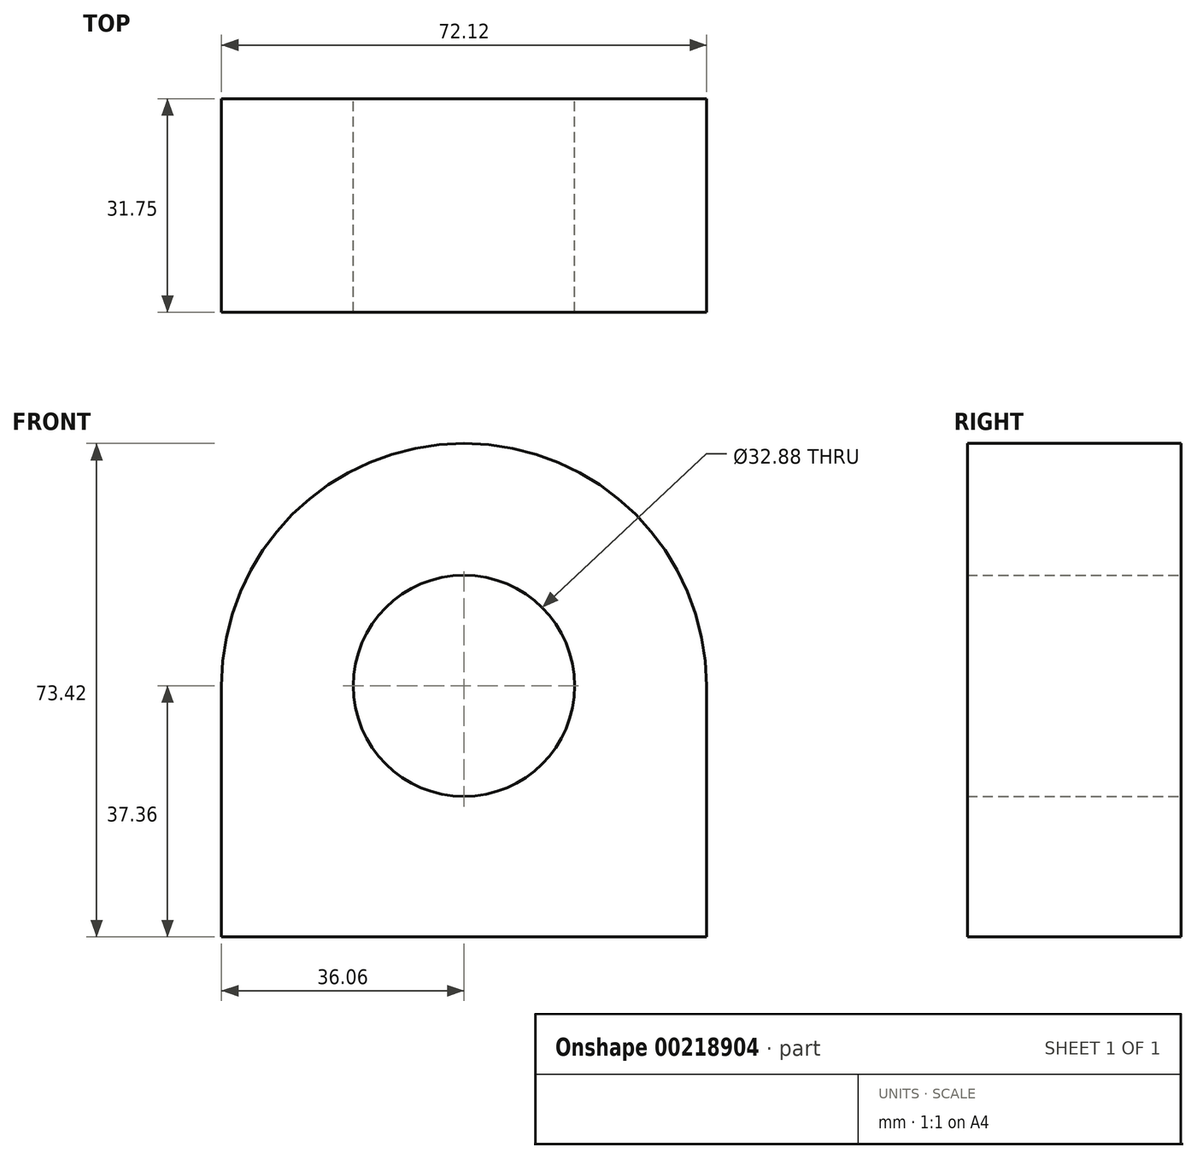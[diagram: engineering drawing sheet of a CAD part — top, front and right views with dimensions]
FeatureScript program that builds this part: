
annotation { "Feature Type Name" : "Feature", "Feature Type Description" : "" }
export const myFeature = defineFeature(function(context is Context, id is Id, definition is map)
    precondition{}
    {
        {
            var Q0;
            Q0=qCreatedBy(makeId("Front.planeOp"),FACE);
            var sketch = newSketch(context, id + "F0", { "sketchPlane" : qUnion([Q0])});
            skLineSegment(sketch, "E0.top", {"start": v(36.06, -18.68) * mm, "end": v(-36.06, -18.68) * mm});
            skLineSegment(sketch, "E0.left", {"start": v(36.06, 18.68) * mm, "end": v(36.06, -18.68) * mm});
            skLineSegment(sketch, "E0.right", {"start": v(-36.06, 18.68) * mm, "end": v(-36.06, -18.68) * mm});
            skPoint(sketch, "E0.middle", {"position": v(0, 0) * mm});
            skArc(sketch, "E1", {"start": v(-36.06, 18.68) * mm, "mid": v(0, 54.74) * mm, "end": v(36.06, 18.68) * mm});
            skCircle(sketch, "E2", {"center": v(0, 18.68) * mm, "radius": 16.44 * mm});
            skSolve(sketch);
        }
        {
            var Q0;
            Q0=makeQuery(id+"F0.imprint","IMPRINT",FACE,{"disambiguationData":[TD([[makeQuery(id+"F0.imprint","IMPRINT",EDGE,{"derivedFrom":sQuery(id+"F0.wireOp",EDGE,"E0.top")}),-1.0]])]});
            extrude(context, id + "F1", {"entities" : qUnion([Q0]), "depth" : 31.75 * mm});
        }
    });
